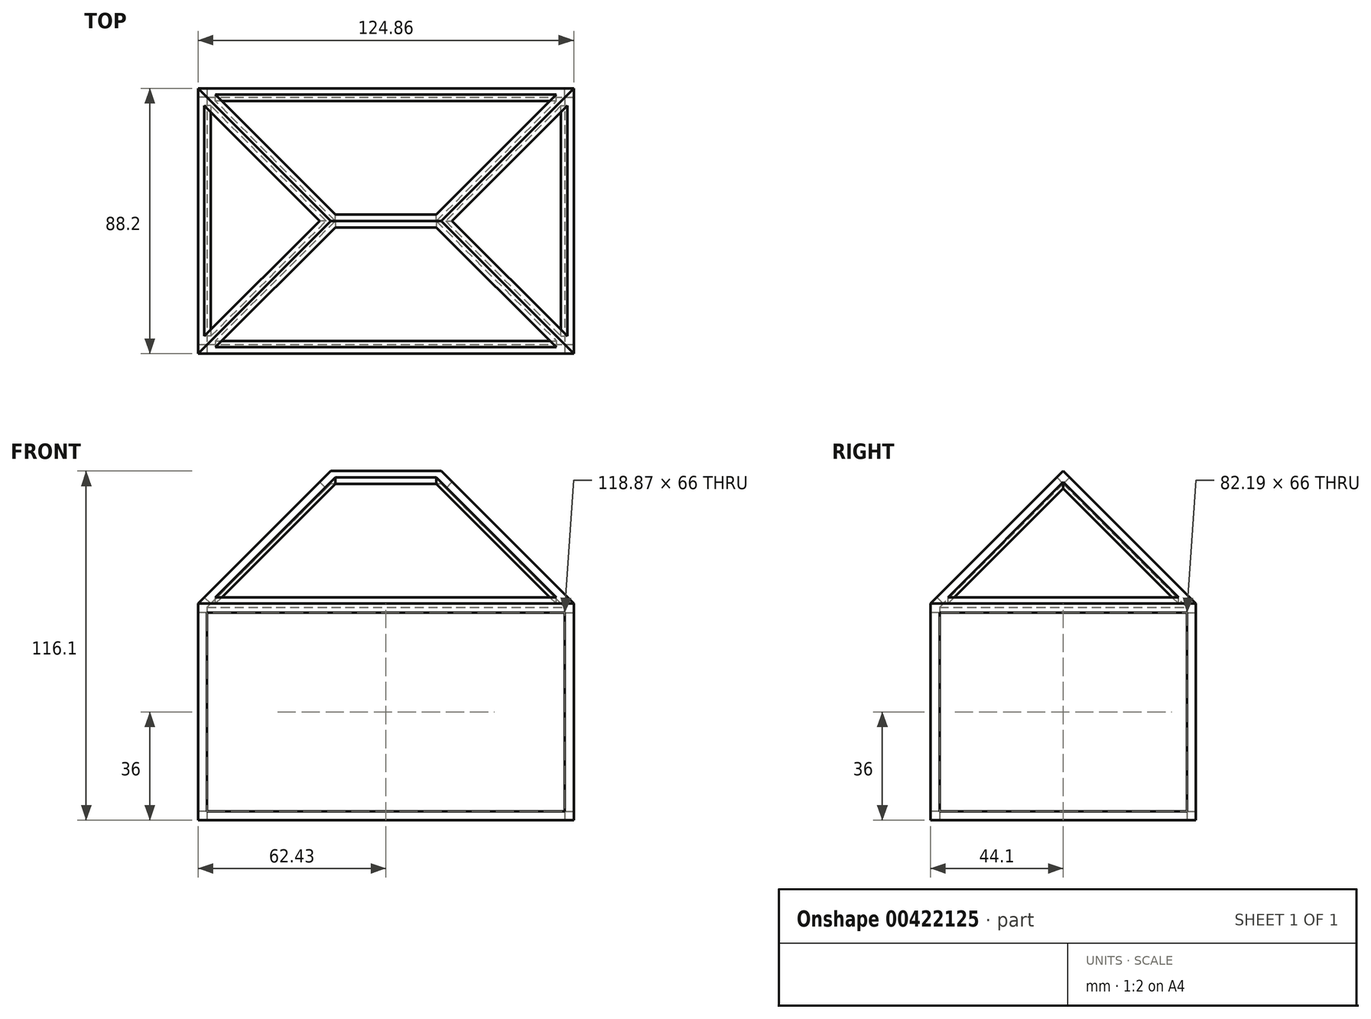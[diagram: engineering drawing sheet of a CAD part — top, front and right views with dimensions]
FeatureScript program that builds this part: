
annotation { "Feature Type Name" : "Feature", "Feature Type Description" : "" }
export const myFeature = defineFeature(function(context is Context, id is Id, definition is map)
    precondition{}
    {
        {
            var Q0;
            Q0=qCreatedBy(makeId("Top.planeOp"),FACE);
            var sketch = newSketch(context, id + "F0", { "sketchPlane" : qUnion([Q0])});
            skLineSegment(sketch, "E0.bottom", {"start": v(-62.43, 44.1) * mm, "end": v(62.43, 44.1) * mm});
            skLineSegment(sketch, "E0.top", {"start": v(-62.43, -44.1) * mm, "end": v(62.43, -44.1) * mm});
            skLineSegment(sketch, "E0.left", {"start": v(-62.43, 44.1) * mm, "end": v(-62.43, -44.1) * mm});
            skLineSegment(sketch, "E0.right", {"start": v(62.43, 44.1) * mm, "end": v(62.43, -44.1) * mm});
            skPoint(sketch, "E0.middle", {"position": v(0, 0) * mm});
            skSolve(sketch);
        }
        {
            var Q0;
            Q0=qSketchRegion(id+"F0",true);
            extrude(context, id + "F1", {"entities" : qUnion([Q0]), "depth" : 72 * mm});
        }
        {
            var Q0;
            Q0=makeQuery(id+"F1.opExtrude","CAP_FACE",FACE,{"disambiguationData":[OSD([sQuery(id+"F0.wireOp",EDGE,"E0.bottom"),sQuery(id+"F0.wireOp",EDGE,"E0.top"),sQuery(id+"F0.wireOp",EDGE,"E0.left"),sQuery(id+"F0.wireOp",EDGE,"E0.right")])],"isStart":false});
            extrude(context, id + "F2", {"entities" : qUnion([Q0]), "operationType" : NewBodyOperationType.ADD, "endBound" : BoundingType.THROUGH_ALL, "depth" : 25 * mm, "hasDraft" : true, "draftAngle" : 45 * degree, "draftPullDirection" : true});
        }
        {
            assignVariable(context, id + "F3", {"name" : "depth", "anyValue" : 3});
        }
        {
            var Q0;
            Q0=makeQuery(id+"F2.opExtrude","SWEPT_FACE",FACE,{"disambiguationData":[OSD([sQuery(id+"F0.wireOp",EDGE,"E0.top")])]});
            var Q1;
            Q1=makeQuery(id+"F1.opExtrude","SWEPT_BODY",BODY,{"disambiguationData":[OSD([sQuery(id+"F0.wireOp",EDGE,"E0.bottom"),sQuery(id+"F0.wireOp",EDGE,"E0.top"),sQuery(id+"F0.wireOp",EDGE,"E0.left"),sQuery(id+"F0.wireOp",EDGE,"E0.right")])]});
            shell(context, id + "F4", {"isHollow" : true, "entities" : qUnion([Q0]), "parts" : qUnion([Q1]), "thickness" : (getVariable(context, 'depth')) * mm});
        }
        {
            var Q0;
            Q0=makeQuery(id+"F1.opExtrude","SWEPT_FACE",FACE,{"disambiguationData":[OSD([sQuery(id+"F0.wireOp",EDGE,"E0.top")])]});
            var sketch = newSketch(context, id + "F5", { "sketchPlane" : qUnion([Q0])});
            skLineSegment(sketch, "E1.0", {"start": v(-59.43, 3) * mm, "end": v(59.43, 3) * mm});
            skLineSegment(sketch, "E1.1", {"start": v(-59.43, 69) * mm, "end": v(-59.43, 3) * mm});
            skLineSegment(sketch, "E1.2", {"start": v(59.43, 69) * mm, "end": v(-59.43, 69) * mm});
            skLineSegment(sketch, "E1.3", {"start": v(59.43, 3) * mm, "end": v(59.43, 69) * mm});
            skSolve(sketch);
        }
        {
            var Q0;
            Q0=makeQuery(id+"F1.opExtrude","SWEPT_FACE",FACE,{"disambiguationData":[OSD([sQuery(id+"F0.wireOp",EDGE,"E0.right")])]});
            var sketch = newSketch(context, id + "F6", { "sketchPlane" : qUnion([Q0])});
            skLineSegment(sketch, "E2.0", {"start": v(-41.1, 3) * mm, "end": v(41.1, 3) * mm});
            skLineSegment(sketch, "E2.1", {"start": v(-41.1, 69) * mm, "end": v(-41.1, 3) * mm});
            skLineSegment(sketch, "E2.2", {"start": v(41.1, 69) * mm, "end": v(-41.1, 69) * mm});
            skLineSegment(sketch, "E2.3", {"start": v(41.1, 3) * mm, "end": v(41.1, 69) * mm});
            skSolve(sketch);
        }
        {
            var Q0;
            Q0=makeQuery(id+"F2.opExtrude","SWEPT_FACE",FACE,{"disambiguationData":[OSD([sQuery(id+"F0.wireOp",EDGE,"E0.top")])]});
            var sketch = newSketch(context, id + "F7", { "sketchPlane" : qUnion([Q0])});
            skLineSegment(sketch, "E3.0", {"start": v(-16.78, 79.1) * mm, "end": v(16.78, 79.1) * mm});
            skLineSegment(sketch, "E3.1", {"start": v(-16.78, 79.1) * mm, "end": v(-56.64, 22.73) * mm});
            skLineSegment(sketch, "E3.2", {"start": v(-56.64, 22.73) * mm, "end": v(56.64, 22.73) * mm});
            skLineSegment(sketch, "E3.3", {"start": v(16.78, 79.1) * mm, "end": v(56.64, 22.73) * mm});
            skSolve(sketch);
        }
        {
            var Q0;
            Q0=makeQuery(id+"F2.opExtrude","SWEPT_FACE",FACE,{"disambiguationData":[OSD([sQuery(id+"F0.wireOp",EDGE,"E0.left")])]});
            var sketch = newSketch(context, id + "F8", { "sketchPlane" : qUnion([Q0])});
            skLineSegment(sketch, "E4.0", {"start": v(-38.3, 9.76) * mm, "end": v(38.3, 9.76) * mm});
            skLineSegment(sketch, "E4.1", {"start": v(0, 63.93) * mm, "end": v(-38.3, 9.76) * mm});
            skLineSegment(sketch, "E4.2", {"start": v(38.3, 9.76) * mm, "end": v(0, 63.93) * mm});
            skSolve(sketch);
        }
        {
            var Q0;
            Q0=makeQuery(id+"F1.opExtrude","SWEPT_FACE",FACE,{"disambiguationData":[OSD([sQuery(id+"F0.wireOp",EDGE,"E0.left")])]});
            var sketch = newSketch(context, id + "F9", { "sketchPlane" : qUnion([Q0])});
            skLineSegment(sketch, "E5.0", {"start": v(-41.1, 3) * mm, "end": v(41.1, 3) * mm});
            skLineSegment(sketch, "E5.1", {"start": v(-41.1, 69) * mm, "end": v(-41.1, 3) * mm});
            skLineSegment(sketch, "E5.2", {"start": v(41.1, 69) * mm, "end": v(-41.1, 69) * mm});
            skLineSegment(sketch, "E5.3", {"start": v(41.1, 3) * mm, "end": v(41.1, 69) * mm});
            skSolve(sketch);
        }
        {
            var Q0;
            Q0=makeQuery(id+"F2.opExtrude","SWEPT_FACE",FACE,{"disambiguationData":[OSD([sQuery(id+"F0.wireOp",EDGE,"E0.bottom")])]});
            var sketch = newSketch(context, id + "F10", { "sketchPlane" : qUnion([Q0])});
            skLineSegment(sketch, "E6.0", {"start": v(16.78, 79.1) * mm, "end": v(56.64, 22.73) * mm});
            skLineSegment(sketch, "E6.1", {"start": v(16.78, 79.1) * mm, "end": v(-16.78, 79.1) * mm});
            skLineSegment(sketch, "E6.2", {"start": v(-16.78, 79.1) * mm, "end": v(-56.64, 22.73) * mm});
            skLineSegment(sketch, "E6.3", {"start": v(-56.64, 22.73) * mm, "end": v(56.64, 22.73) * mm});
            skSolve(sketch);
        }
        {
            var Q0;
            Q0=makeQuery(id+"F2.opExtrude","SWEPT_FACE",FACE,{"disambiguationData":[OSD([sQuery(id+"F0.wireOp",EDGE,"E0.right")])]});
            var sketch = newSketch(context, id + "F11", { "sketchPlane" : qUnion([Q0])});
            skLineSegment(sketch, "E7.0", {"start": v(-38.3, 9.76) * mm, "end": v(38.3, 9.76) * mm});
            skLineSegment(sketch, "E7.1", {"start": v(0, 63.93) * mm, "end": v(-38.3, 9.76) * mm});
            skLineSegment(sketch, "E7.2", {"start": v(38.3, 9.76) * mm, "end": v(0, 63.93) * mm});
            skSolve(sketch);
        }
        {
            var Q0;
            Q0=makeQuery(id+"F1.opExtrude","SWEPT_FACE",FACE,{"disambiguationData":[OSD([sQuery(id+"F0.wireOp",EDGE,"E0.bottom")])]});
            var sketch = newSketch(context, id + "F12", { "sketchPlane" : qUnion([Q0])});
            skLineSegment(sketch, "E8.0", {"start": v(-59.43, 3) * mm, "end": v(59.43, 3) * mm});
            skLineSegment(sketch, "E8.1", {"start": v(-59.43, 69) * mm, "end": v(-59.43, 3) * mm});
            skLineSegment(sketch, "E8.2", {"start": v(59.43, 69) * mm, "end": v(-59.43, 69) * mm});
            skLineSegment(sketch, "E8.3", {"start": v(59.43, 3) * mm, "end": v(59.43, 69) * mm});
            skSolve(sketch);
        }
        {
            var Q0;
            Q0=makeQuery(id+"F1.opExtrude","CAP_FACE",FACE,{"disambiguationData":[OSD([sQuery(id+"F0.wireOp",EDGE,"E0.bottom"),sQuery(id+"F0.wireOp",EDGE,"E0.top"),sQuery(id+"F0.wireOp",EDGE,"E0.left"),sQuery(id+"F0.wireOp",EDGE,"E0.right")])],"isStart":true});
            var sketch = newSketch(context, id + "F13", { "sketchPlane" : qUnion([Q0])});
            skLineSegment(sketch, "E9.0", {"start": v(-59.43, 41.1) * mm, "end": v(-59.43, -41.1) * mm});
            skLineSegment(sketch, "E9.1", {"start": v(59.43, 41.1) * mm, "end": v(-59.43, 41.1) * mm});
            skLineSegment(sketch, "E9.2", {"start": v(59.43, -41.1) * mm, "end": v(59.43, 41.1) * mm});
            skLineSegment(sketch, "E9.3", {"start": v(-59.43, -41.1) * mm, "end": v(59.43, -41.1) * mm});
            skSolve(sketch);
        }
        {
            var Q0;
            Q0=makeQuery(id+"F6.imprint","IMPRINT",FACE,{"disambiguationData":[TD([[makeQuery(id+"F6.imprint","IMPRINT",EDGE,{"derivedFrom":sQuery(id+"F6.wireOp",EDGE,"E2.0")}),1.0]])]});
            extrude(context, id + "F14", {"entities" : qUnion([Q0]), "operationType" : NewBodyOperationType.REMOVE, "oppositeDirection" : true, "depth" : (getVariable(context, 'depth') + 2) * mm});
        }
        {
            var Q0;
            Q0=makeQuery(id+"F12.imprint","IMPRINT",FACE,{"disambiguationData":[TD([[makeQuery(id+"F12.imprint","IMPRINT",EDGE,{"derivedFrom":sQuery(id+"F12.wireOp",EDGE,"E8.0")}),1.0]])]});
            extrude(context, id + "F15", {"entities" : qUnion([Q0]), "operationType" : NewBodyOperationType.REMOVE, "oppositeDirection" : true, "depth" : (getVariable(context, 'depth') + 2) * mm});
        }
        {
            var Q0;
            Q0=makeQuery(id+"F9.imprint","IMPRINT",FACE,{"disambiguationData":[TD([[makeQuery(id+"F9.imprint","IMPRINT",EDGE,{"derivedFrom":sQuery(id+"F9.wireOp",EDGE,"E5.0")}),1.0]])]});
            extrude(context, id + "F16", {"entities" : qUnion([Q0]), "operationType" : NewBodyOperationType.REMOVE, "oppositeDirection" : true, "depth" : (getVariable(context, 'depth') + 2) * mm});
        }
        {
            var Q0;
            Q0=makeQuery(id+"F5.imprint","IMPRINT",FACE,{"disambiguationData":[TD([[makeQuery(id+"F5.imprint","IMPRINT",EDGE,{"derivedFrom":sQuery(id+"F5.wireOp",EDGE,"E1.0")}),1.0]])]});
            extrude(context, id + "F17", {"entities" : qUnion([Q0]), "operationType" : NewBodyOperationType.REMOVE, "oppositeDirection" : true, "depth" : (getVariable(context, 'depth') + 2) * mm});
        }
        {
            var Q0;
            Q0=makeQuery(id+"F13.imprint","IMPRINT",FACE,{"disambiguationData":[TD([[makeQuery(id+"F13.imprint","IMPRINT",EDGE,{"derivedFrom":sQuery(id+"F13.wireOp",EDGE,"E9.0")}),1.0]])]});
            extrude(context, id + "F18", {"entities" : qUnion([Q0]), "operationType" : NewBodyOperationType.REMOVE, "oppositeDirection" : true, "depth" : (getVariable(context, 'depth') + 2) * mm});
        }
        {
            var Q0;
            Q0=makeQuery(id+"F7.imprint","IMPRINT",FACE,{"disambiguationData":[TD([[makeQuery(id+"F7.imprint","IMPRINT",EDGE,{"derivedFrom":sQuery(id+"F7.wireOp",EDGE,"E3.0")}),-1.0]])]});
            extrude(context, id + "F19", {"entities" : qUnion([Q0]), "operationType" : NewBodyOperationType.REMOVE, "oppositeDirection" : true, "depth" : (getVariable(context, 'depth') + 2) * mm});
        }
        {
            var Q0;
            Q0=makeQuery(id+"F8.imprint","IMPRINT",FACE,{"disambiguationData":[TD([[makeQuery(id+"F8.imprint","IMPRINT",EDGE,{"derivedFrom":sQuery(id+"F8.wireOp",EDGE,"E4.0")}),1.0]])]});
            extrude(context, id + "F20", {"entities" : qUnion([Q0]), "operationType" : NewBodyOperationType.REMOVE, "oppositeDirection" : true, "depth" : (getVariable(context, 'depth') + 2) * mm});
        }
        {
            var Q0;
            Q0=makeQuery(id+"F10.imprint","IMPRINT",FACE,{"disambiguationData":[TD([[makeQuery(id+"F10.imprint","IMPRINT",EDGE,{"derivedFrom":sQuery(id+"F10.wireOp",EDGE,"E6.0")}),-1.0]])]});
            extrude(context, id + "F21", {"entities" : qUnion([Q0]), "operationType" : NewBodyOperationType.REMOVE, "oppositeDirection" : true, "depth" : (getVariable(context, 'depth') + 2) * mm});
        }
        {
            var Q0;
            Q0=makeQuery(id+"F11.imprint","IMPRINT",FACE,{"disambiguationData":[TD([[makeQuery(id+"F11.imprint","IMPRINT",EDGE,{"derivedFrom":sQuery(id+"F11.wireOp",EDGE,"E7.0")}),1.0]])]});
            extrude(context, id + "F22", {"entities" : qUnion([Q0]), "operationType" : NewBodyOperationType.REMOVE, "oppositeDirection" : true, "depth" : (getVariable(context, 'depth') + 2) * mm});
        }
    });
